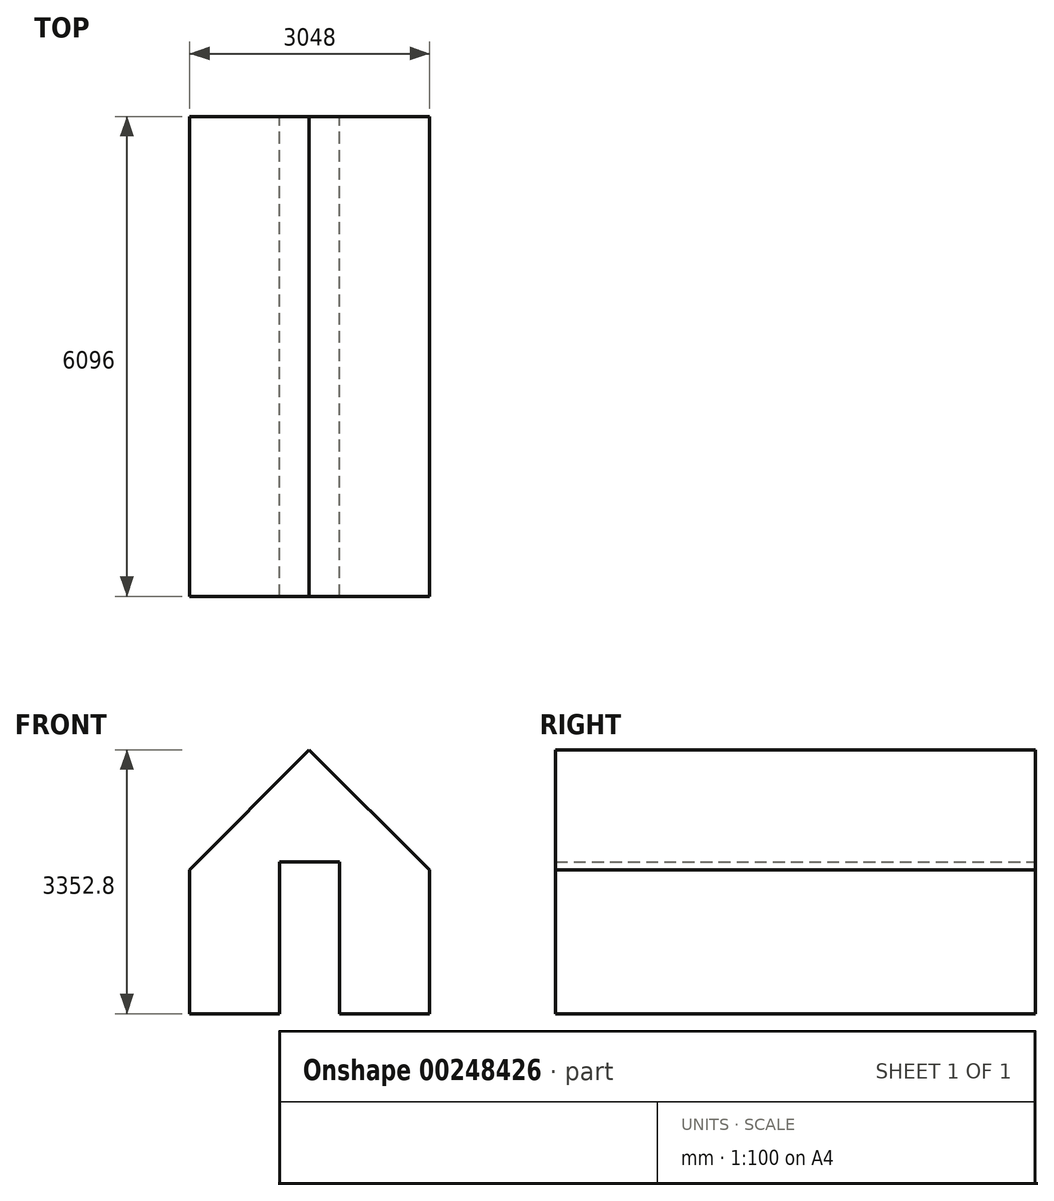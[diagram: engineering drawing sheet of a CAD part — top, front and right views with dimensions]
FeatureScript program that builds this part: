
annotation { "Feature Type Name" : "Feature", "Feature Type Description" : "" }
export const myFeature = defineFeature(function(context is Context, id is Id, definition is map)
    precondition{}
    {
        {
            var Q0;
            Q0=qCreatedBy(makeId("Front.planeOp"),FACE);
            var sketch = newSketch(context, id + "F0", { "sketchPlane" : qUnion([Q0])});
            skLineSegment(sketch, "E0.bottom", {"start": v(-1516.18, 861.71) * mm, "end": v(1531.82, 861.71) * mm});
            skLineSegment(sketch, "E0.top", {"start": v(-1516.18, -967.09) * mm, "end": v(1531.82, -967.09) * mm});
            skLineSegment(sketch, "E0.left", {"start": v(-1516.18, 861.71) * mm, "end": v(-1516.18, -967.09) * mm});
            skLineSegment(sketch, "E0.right", {"start": v(1531.82, 861.71) * mm, "end": v(1531.82, -967.09) * mm});
            skLineSegment(sketch, "E1", {"start": v(0, 861.71) * mm, "end": v(0, 2385.71) * mm});
            skLineSegment(sketch, "E2", {"start": v(0, 2385.71) * mm, "end": v(-1516.18, 861.71) * mm});
            skLineSegment(sketch, "E3", {"start": v(0, 2385.71) * mm, "end": v(1531.82, 861.71) * mm});
            skLineSegment(sketch, "E4.bottom", {"start": v(7.82, -967.09) * mm, "end": v(-373.18, -967.09) * mm});
            skLineSegment(sketch, "E4.top", {"start": v(7.82, 963.31) * mm, "end": v(-373.18, 963.31) * mm});
            skLineSegment(sketch, "E4.left", {"start": v(7.82, -967.09) * mm, "end": v(7.82, 963.31) * mm});
            skLineSegment(sketch, "E4.right", {"start": v(-373.18, -967.09) * mm, "end": v(-373.18, 963.31) * mm});
            skLineSegment(sketch, "E5.bottom", {"start": v(7.82, 963.31) * mm, "end": v(388.82, 963.31) * mm});
            skLineSegment(sketch, "E5.top", {"start": v(7.82, -967.09) * mm, "end": v(388.82, -967.09) * mm});
            skLineSegment(sketch, "E5.left", {"start": v(7.82, 963.31) * mm, "end": v(7.82, -967.09) * mm});
            skLineSegment(sketch, "E5.right", {"start": v(388.82, 963.31) * mm, "end": v(388.82, -967.09) * mm});
            skSolve(sketch);
        }
        {
            var Q0;
            {var subQ0=sQuery(id+"F0.wireOp",EDGE,"E0.left");Q0=makeQuery(id+"F0.imprint","IMPRINT",FACE,{"disambiguationData":[TD([[makeQuery(id+"F0.imprint","IMPRINT",EDGE,{"derivedFrom":subQ0}),1.0]])]});}
            var Q1;
            {var subQ0=sQuery(id+"F0.wireOp",EDGE,"E0.right");Q1=makeQuery(id+"F0.imprint","IMPRINT",FACE,{"disambiguationData":[TD([[makeQuery(id+"F0.imprint","IMPRINT",EDGE,{"derivedFrom":subQ0}),-1.0]])]});}
            var Q2;
            {var subQ5=sQuery(id+"F0.wireOp",EDGE,"E2");Q2=makeQuery(id+"F0.imprint","IMPRINT",FACE,{"disambiguationData":[TD([[makeQuery(id+"F0.imprint","IMPRINT",EDGE,{"derivedFrom":subQ5}),1.0]])]});}
            var Q3;
            {var subQ4=sQuery(id+"F0.wireOp",EDGE,"E3");Q3=makeQuery(id+"F0.imprint","IMPRINT",FACE,{"disambiguationData":[TD([[makeQuery(id+"F0.imprint","IMPRINT",EDGE,{"derivedFrom":subQ4}),-1.0]])]});}
            extrude(context, id + "F1", {"entities" : qUnion([Q0, Q1, Q2, Q3]), "depth" : 6096 * mm});
        }
    });
